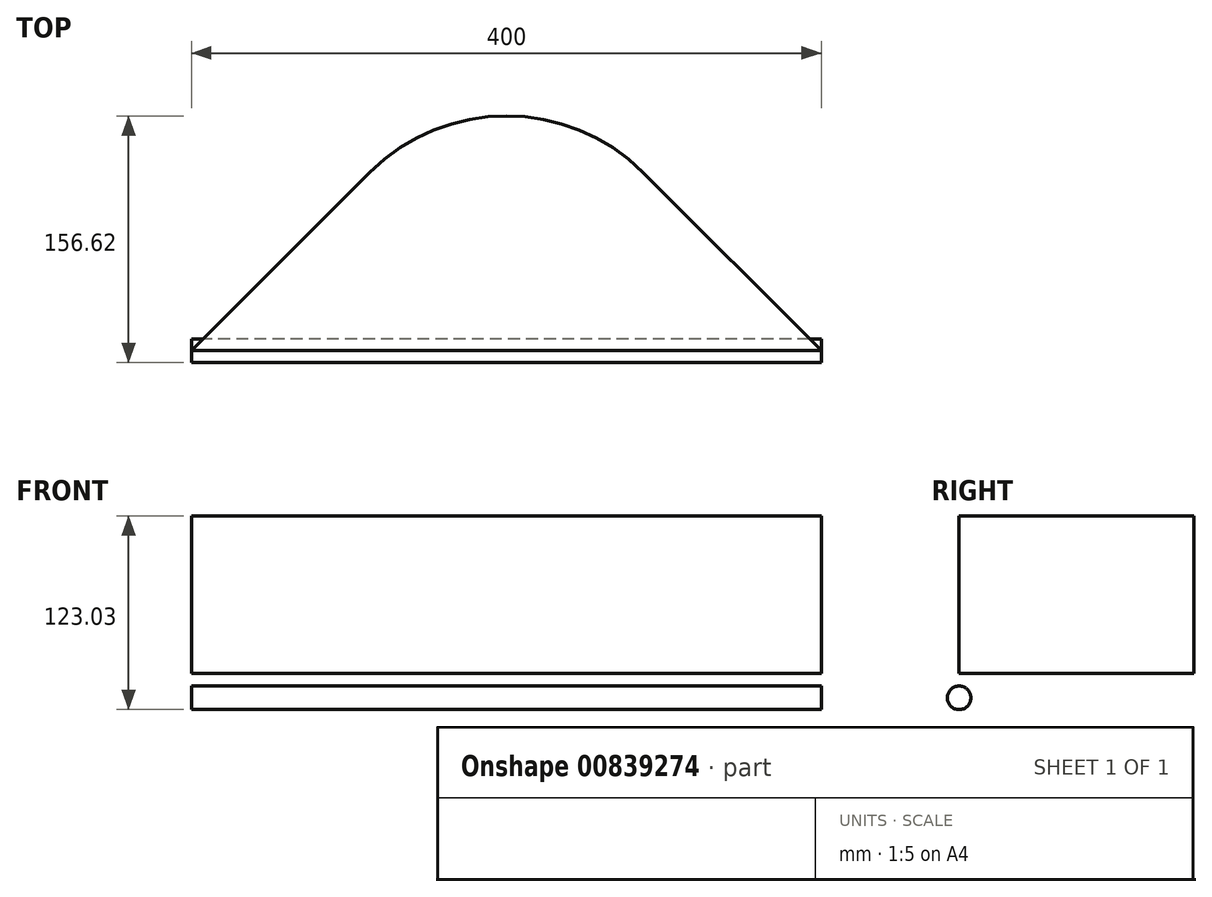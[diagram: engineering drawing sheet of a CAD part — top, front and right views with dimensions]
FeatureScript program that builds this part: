
annotation { "Feature Type Name" : "Feature", "Feature Type Description" : "" }
export const myFeature = defineFeature(function(context is Context, id is Id, definition is map)
    precondition{}
    {
        {
            var Q0;
            Q0=qCreatedBy(makeId("Top.planeOp"),FACE);
            var sketch = newSketch(context, id + "F0", { "sketchPlane" : qUnion([Q0])});
            skLineSegment(sketch, "E0", {"start": v(0, 0) * mm, "end": v(400, 0) * mm});
            skLineSegment(sketch, "E1", {"start": v(400, 0) * mm, "end": v(286.86, 113.14) * mm});
            skLineSegment(sketch, "E2", {"start": v(0, 0) * mm, "end": v(113.14, 113.14) * mm});
            skArc(sketch, "E3", {"start": v(286.86, 113.14) * mm, "mid": v(200, 149.12) * mm, "end": v(113.14, 113.14) * mm});
            skSolve(sketch);
        }
        {
            var Q0;
            Q0 = qSketchRegion(id + "F0", true);
            extrude(context, id + "F1", {"entities" : qUnion([Q0]), "oppositeDirection" : true, "depth" : 100 * mm, "offsetDistance" : 25 * mm});
        }
        {
            var Q0;
            Q0=qCreatedBy(makeId("Right.planeOp"),FACE);
            var sketch = newSketch(context, id + "F2", { "sketchPlane" : qUnion([Q0])});
            skCircle(sketch, "E4", {"center": v(0, -115.53) * mm, "radius": 7.5 * mm});
            skSolve(sketch);
        }
        {
            var Q0;
            Q0 = qSketchRegion(id + "F2", true);
            extrude(context, id + "F3", {"entities" : qUnion([Q0]), "depth" : 400 * mm, "offsetDistance" : 25 * mm});
        }
    });
